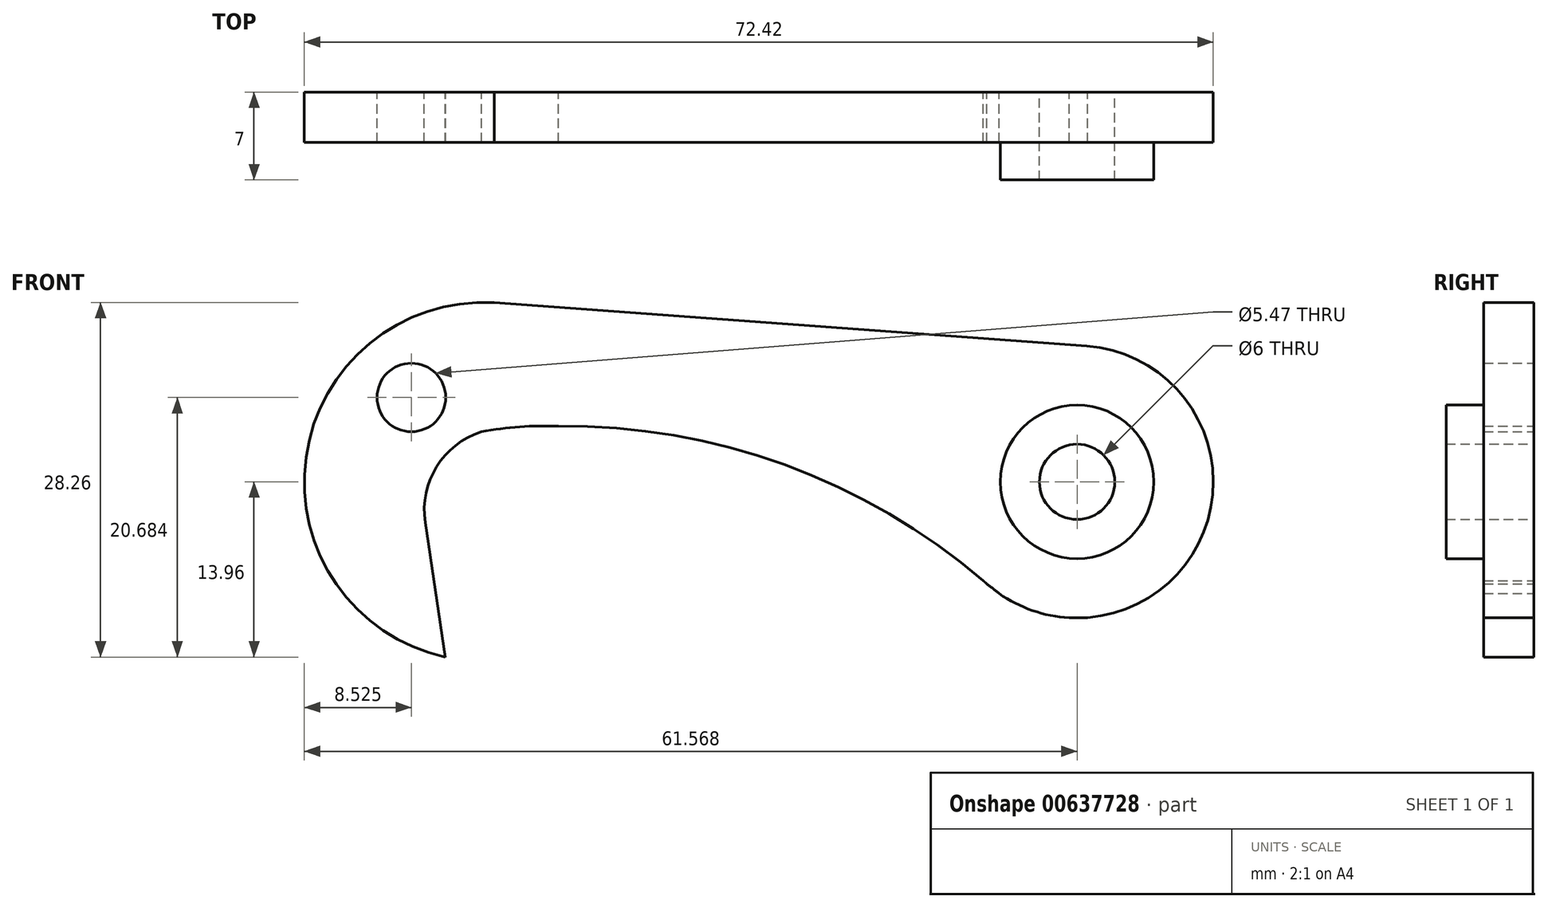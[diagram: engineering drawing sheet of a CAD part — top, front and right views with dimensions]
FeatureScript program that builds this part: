
annotation { "Feature Type Name" : "Feature", "Feature Type Description" : "" }
export const myFeature = defineFeature(function(context is Context, id is Id, definition is map)
    precondition{}
    {
        {
            var Q0;
            Q0=qCreatedBy(makeId("Front.planeOp"),FACE);
            var sketch = newSketch(context, id + "F0", { "sketchPlane" : qUnion([Q0])});
            skCircle(sketch, "E0", {"center": v(12.6, 0) * mm, "radius": 10.85 * mm});
            skLineSegment(sketch, "E1", {"start": v(-33.85, 14.27) * mm, "end": v(13.39, 10.82) * mm});
            skLineSegment(sketch, "E2", {"start": v(11.97, -10.83) * mm, "end": v(13.45, -10.82) * mm});
            skArc(sketch, "E3", {"start": v(-20.93, 3.92) * mm, "mid": v(-45.1, 9.8) * mm, "end": v(-37.74, -13.96) * mm});
            skArc(sketch, "E4", {"start": v(-28.71, 4.43) * mm, "mid": v(-31.8, 4.39) * mm, "end": v(-34.87, 4) * mm});
            skArc(sketch, "E5", {"start": v(-34.87, 4) * mm, "mid": v(-38.43, 1.2) * mm, "end": v(-39.34, -3.23) * mm});
            skLineSegment(sketch, "E6", {"start": v(-39.34, -3.23) * mm, "end": v(-37.74, -13.96) * mm});
            skPoint(sketch, "E7.start.orphan", {"position": v(-34.68, -14.3) * mm});
            skCircle(sketch, "E8", {"center": v(12.6, 0) * mm, "radius": 3 * mm});
            skArc(sketch, "E9", {"start": v(6.38, -8.9) * mm, "mid": v(5.9, -8.51) * mm, "end": v(5.42, -8.14) * mm});
            skArc(sketch, "E10", {"start": v(5.13, -7.88) * mm, "mid": v(-10.67, 1.35) * mm, "end": v(-28.71, 4.43) * mm});
            skCircle(sketch, "E11", {"center": v(-40.44, 6.72) * mm, "radius": 2.73 * mm});
            skSolve(sketch);
        }
        {
            var Q0;
            {var subQ0=sQuery(id+"F0.wireOp",EDGE,"E4");Q0=makeQuery(id+"F0.imprint","IMPRINT",FACE,{"disambiguationData":[TD([[makeQuery(id+"F0.imprint","IMPRINT",EDGE,{"derivedFrom":subQ0}),-1.0]])]});}
            var Q1;
            {var subQ0=sQuery(id+"F0.wireOp",EDGE,"E1");var subQ1=sQuery(id+"F0.wireOp",EDGE,"E0");var subQ2=makeQuery(id+"F0.imprint","INTERSECT",VERTEX,{"derivedFrom":[subQ1,subQ0]});Q1=makeQuery(id+"F0.imprint","IMPRINT",FACE,{"disambiguationData":[TD([[makeQuery(id+"F0.imprint","IMPRINT",EDGE,{"disambiguationData":[TD([[subQ2,-1.0]])],"derivedFrom":subQ1}),-1.0]])]});}
            var Q2;
            {var subQ0=sQuery(id+"F0.wireOp",EDGE,"E2");Q2=makeQuery(id+"F0.imprint","IMPRINT",FACE,{"disambiguationData":[TD([[makeQuery(id+"F0.imprint","IMPRINT",EDGE,{"derivedFrom":subQ0}),1.0]])]});}
            extrude(context, id + "F1", {"entities" : qUnion([Q0, Q1, Q2]), "depth" : 4 * mm, "offsetDistance" : 25 * mm});
        }
        {
            var Q0;
            Q0=makeQuery(id+"F1.opExtrude","CAP_FACE",FACE,{"disambiguationData":[OSD([sQuery(id+"F0.wireOp",EDGE,"E0"),sQuery(id+"F0.wireOp",EDGE,"E1"),sQuery(id+"F0.wireOp",EDGE,"E2"),sQuery(id+"F0.wireOp",EDGE,"E3"),sQuery(id+"F0.wireOp",EDGE,"E4"),sQuery(id+"F0.wireOp",EDGE,"E5"),sQuery(id+"F0.wireOp",EDGE,"E6"),sQuery(id+"F0.wireOp",EDGE,"E8"),sQuery(id+"F0.wireOp",EDGE,"E9"),sQuery(id+"F0.wireOp",EDGE,"E10")])],"isStart":false});
            var sketch = newSketch(context, id + "F2", { "sketchPlane" : qUnion([Q0])});
            skCircle(sketch, "E12", {"center": v(12.6, 0) * mm, "radius": 6.11 * mm});
            skSolve(sketch);
        }
        {
            var Q0;
            Q0=makeQuery(id+"F2.imprint","IMPRINT",FACE,{"disambiguationData":[TD([[makeQuery(id+"F2.imprint","IMPRINT",EDGE,{"derivedFrom":sQuery(id+"F2.wireOp",EDGE,"E12")}),1.0]])]});
            extrude(context, id + "F3", {"entities" : qUnion([Q0]), "operationType" : NewBodyOperationType.ADD, "depth" : 3 * mm, "offsetDistance" : 25 * mm});
        }
    });
